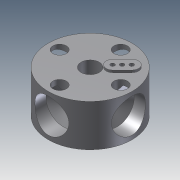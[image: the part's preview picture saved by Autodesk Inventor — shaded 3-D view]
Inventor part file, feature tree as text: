
AUTODESK INVENTOR PART (.ipt)
format: ipt  version: 2011 (Build 150239000, 239)  size: 200,704 bytes
history: native  units: mm
features: sketch x5, hole x4, extrude x3, pattern_circular x2, other x1
ambient origin geometry x8: Origin, YZ Plane, XZ Plane, XY Plane, X Axis, Y Axis, Z Axis, Center Point
feature tree (15):
  sketch  "Sketch2"  dims[d2=37.0mm d3=18.5mm d4=0.0mm]
  extrude  "wheel"  Depth=18.5mm TaperAngle=0.0deg
  hole  "servo mount hole"  [1 undecoded]
  pattern_circular  "servo mount pattern"  Count=4 Angle=360.0deg
  hole  "center install hole"  [1 undecoded]
  hole  "shake wire holes"  [1 undecoded]
  other  "item hole plane"
  hole  "item hole"  [1 undecoded]
  pattern_circular  "item hole patterm"  Count=4 Angle=360.0deg
  extrude  "shake wire support"  Depth=2.0mm
  extrude  "looking holes"  Depth=30.0mm
  sketch  "Sketch4"  dims[d16=45.0deg d17=10.0mm]
  sketch  "Sketch6"  dims[d18=2.2mm d19=6.0mm d20=4.0mm d21=2.0mm d22=90.0deg d23=15.0mm d24=0.0mm d25=40.0mm d26=360.0deg]
  sketch  "Sketch8"  dims[d28=10.0mm d29=10.0mm d30=8.0mm d31=6.0mm d32=4.0mm d33=2.0mm d34=90.0deg d35=15.0mm d36=20.594885mm d37=6.0mm]
  sketch  "Sketch9"  dims[d38=30.0mm d40=3.0mm d41=10.0mm d43=10.0mm d45=1.82mm d46=6.0mm d47=4.0mm d48=2.0mm d49=90.0deg d50=15.0mm d51=0.0mm d55=18.5mm d56=15.0mm d57=6.0mm d58=4.0mm d59=2.0mm d60=90.0deg d61=6.5mm d62=20.594885mm d63=40.0mm d64=360.0deg d66=2.0mm d67=30.0mm d69=3.0mm d70=10.0mm d72=10.0mm d87=1.0mm d88=0.0mm d90=6.0mm d91=40.0mm d93=360.0deg d95=2.0mm d96=10.0mm d97=0.0mm]
note: 4 required parameter values undecoded (feature->parameter linkage not recoverable at this tier; creation-order binding heuristic only, values carry confidence <= 0.55)
